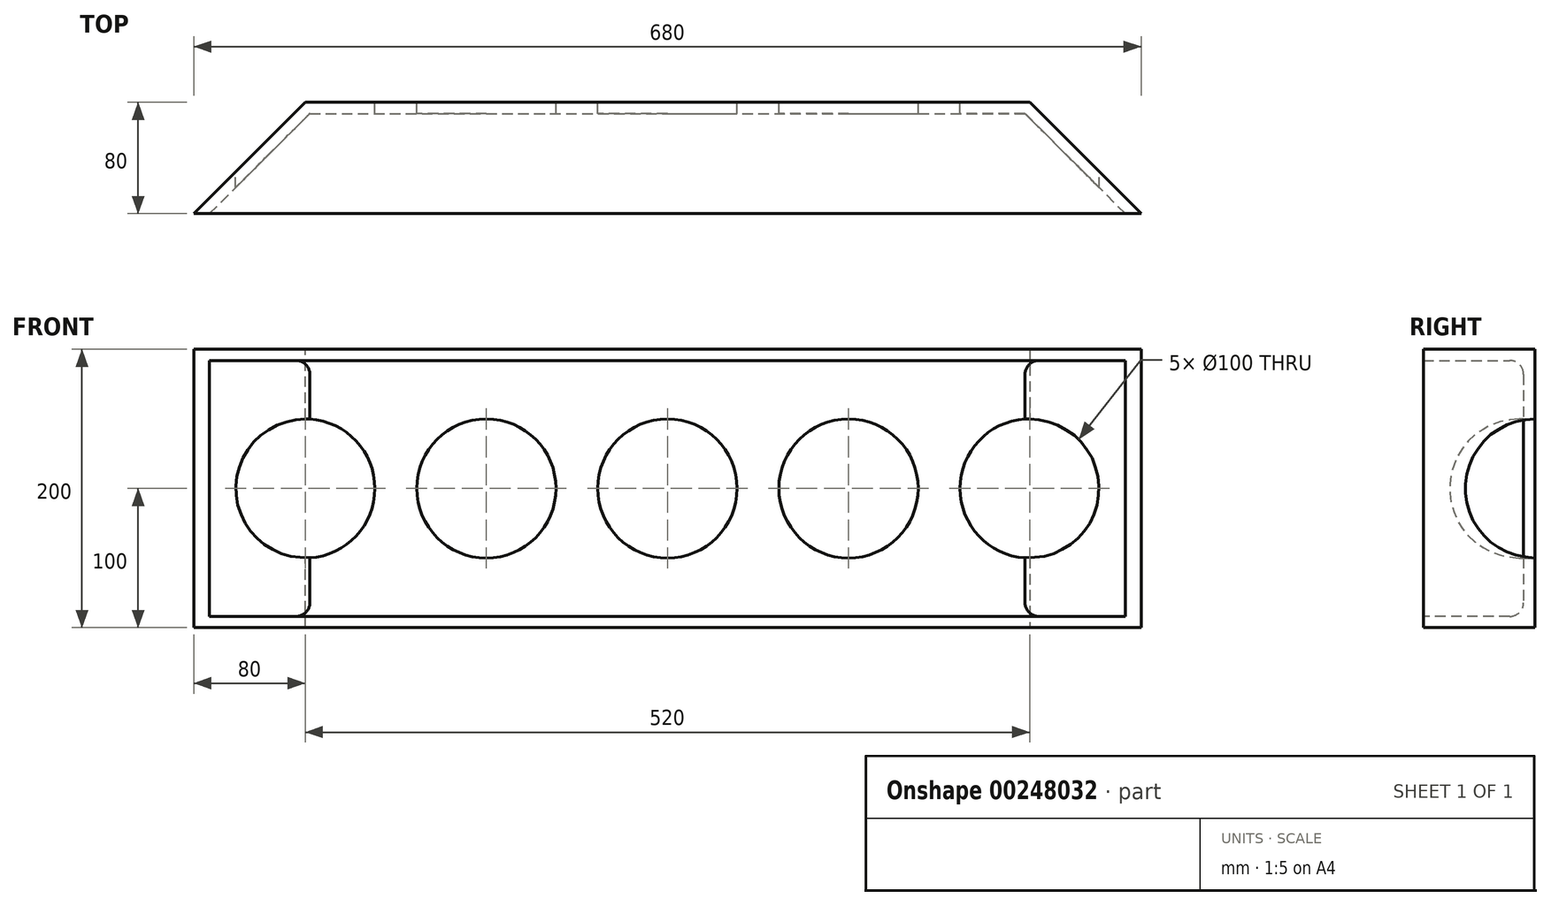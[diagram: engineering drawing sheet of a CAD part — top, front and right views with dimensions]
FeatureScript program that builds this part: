
annotation { "Feature Type Name" : "Feature", "Feature Type Description" : "" }
export const myFeature = defineFeature(function(context is Context, id is Id, definition is map)
    precondition{}
    {
        {
            var Q0;
            Q0=qCreatedBy(makeId("Front.planeOp"),FACE);
            var sketch = newSketch(context, id + "F0", { "sketchPlane" : qUnion([Q0])});
            skLineSegment(sketch, "E0.bottom", {"start": v(-340, 100) * mm, "end": v(340, 100) * mm});
            skLineSegment(sketch, "E0.top", {"start": v(-340, -100) * mm, "end": v(340, -100) * mm});
            skLineSegment(sketch, "E0.left", {"start": v(-340, 100) * mm, "end": v(-340, -100) * mm});
            skLineSegment(sketch, "E0.right", {"start": v(340, 100) * mm, "end": v(340, -100) * mm});
            skPoint(sketch, "E0.middle", {"position": v(0, 0) * mm});
            skSolve(sketch);
        }
        {
            var Q0;
            Q0=makeQuery(id+"F0.imprint","IMPRINT",FACE,{"disambiguationData":[TD([[makeQuery(id+"F0.imprint","IMPRINT",EDGE,{"derivedFrom":sQuery(id+"F0.wireOp",EDGE,"E0.bottom")}),-1.0]])]});
            extrude(context, id + "F1", {"entities" : qUnion([Q0]), "depth" : 80 * mm});
        }
        {
            var Q0;
            Q0=makeQuery(id+"F1.opExtrude","CAP_EDGE",EDGE,{"disambiguationData":[OSD([sQuery(id+"F0.wireOp",EDGE,"E0.left")])],"isStart":true});
            var Q1;
            Q1=makeQuery(id+"F1.opExtrude","CAP_EDGE",EDGE,{"disambiguationData":[OSD([sQuery(id+"F0.wireOp",EDGE,"E0.right")])],"isStart":true});
            chamfer(context, id + "F2", {"entities" : qUnion([Q0, Q1]), "width" : 80 * mm, "tangentPropagation" : true});
        }
        {
            var Q0;
            Q0=makeQuery(id+"F1.opExtrude","CAP_FACE",FACE,{"disambiguationData":[OSD([sQuery(id+"F0.wireOp",EDGE,"E0.bottom"),sQuery(id+"F0.wireOp",EDGE,"E0.top"),sQuery(id+"F0.wireOp",EDGE,"E0.left"),sQuery(id+"F0.wireOp",EDGE,"E0.right")])],"isStart":false});
            shell(context, id + "F3", {"entities" : qUnion([Q0]), "thickness" : 8 * mm});
        }
        {
            var Q0;
            Q0=makeQuery(id+"F1.opExtrude","CAP_FACE",FACE,{"disambiguationData":[OSD([sQuery(id+"F0.wireOp",EDGE,"E0.bottom"),sQuery(id+"F0.wireOp",EDGE,"E0.top"),sQuery(id+"F0.wireOp",EDGE,"E0.left"),sQuery(id+"F0.wireOp",EDGE,"E0.right")])],"isStart":true});
            var sketch = newSketch(context, id + "F4", { "sketchPlane" : qUnion([Q0])});
            skLineSegment(sketch, "E1.bottom", {"start": v(-260, 100) * mm, "end": v(260, 100) * mm});
            skLineSegment(sketch, "E1.top", {"start": v(-260, -100) * mm, "end": v(260, -100) * mm});
            skLineSegment(sketch, "E1.left", {"start": v(-260, 100) * mm, "end": v(-260, -100) * mm});
            skLineSegment(sketch, "E1.right", {"start": v(260, 100) * mm, "end": v(260, -100) * mm});
            skPoint(sketch, "E2", {"position": v(130, 0) * mm});
            skPoint(sketch, "E2.positionSnap0", {"position": v(260, 0) * mm});
            skPoint(sketch, "E3", {"position": v(0, 0) * mm});
            skPoint(sketch, "E4", {"position": v(-130, 0) * mm});
            skPoint(sketch, "E5", {"position": v(-260, 0) * mm});
            skPoint(sketch, "E6", {"position": v(-216, 0) * mm});
            skSolve(sketch);
        }
        {
            var Q0;
            Q0=sQuery(id+"F4.wireOp",VERTEX,"E2");
            var Q1;
            Q1=sQuery(id+"F4.wireOp",VERTEX,"E3");
            var Q2;
            Q2=sQuery(id+"F4.wireOp",VERTEX,"E4");
            var Q3;
            Q3=sQuery(id+"F4.wireOp",VERTEX,"E2.positionSnap0");
            var Q4;
            Q4=sQuery(id+"F4.wireOp",VERTEX,"E5");
            var Q5;
            Q5=makeQuery(id+"F1.opExtrude","SWEPT_BODY",BODY,{"disambiguationData":[OSD([sQuery(id+"F0.wireOp",EDGE,"E0.bottom"),sQuery(id+"F0.wireOp",EDGE,"E0.top"),sQuery(id+"F0.wireOp",EDGE,"E0.left"),sQuery(id+"F0.wireOp",EDGE,"E0.right")])]});
            hole(context, id + "F5", {"style" : HoleStyle.SIMPLE, "endStyle" : HoleEndStyle.THROUGH, "holeDiameter" : 100 * mm, "tappedDepth" : 12 * mm, "tapClearance" : 3, "locations" : qUnion([Q0, Q1, Q2, Q3, Q4]), "scope" : qUnion([Q5])});
        }
        {
            var Q0;
            {var subQ0=sQuery(id+"F0.wireOp",EDGE,"E0.top");Q0=makeQuery(id+"F3.opShell","OFFSET_EDGE",EDGE,{"disambiguationData":[OSD([subQ0]),TDD([makeQuery(id+"F1.opExtrude","CAP_EDGE",EDGE,{"disambiguationData":[OSD([subQ0])],"isStart":true})])]});}
            var Q1;
            {var subQ0=sQuery(id+"F0.wireOp",EDGE,"E0.bottom");Q1=makeQuery(id+"F3.opShell","OFFSET_EDGE",EDGE,{"disambiguationData":[OSD([subQ0]),TDD([makeQuery(id+"F1.opExtrude","CAP_EDGE",EDGE,{"disambiguationData":[OSD([subQ0])],"isStart":true})])]});}
            fillet(context, id + "F6", {"entities" : qUnion([Q0, Q1]), "radius" : 10 * mm, "tangentPropagation" : true, "allowEdgeOverflow" : false});
        }
    });
